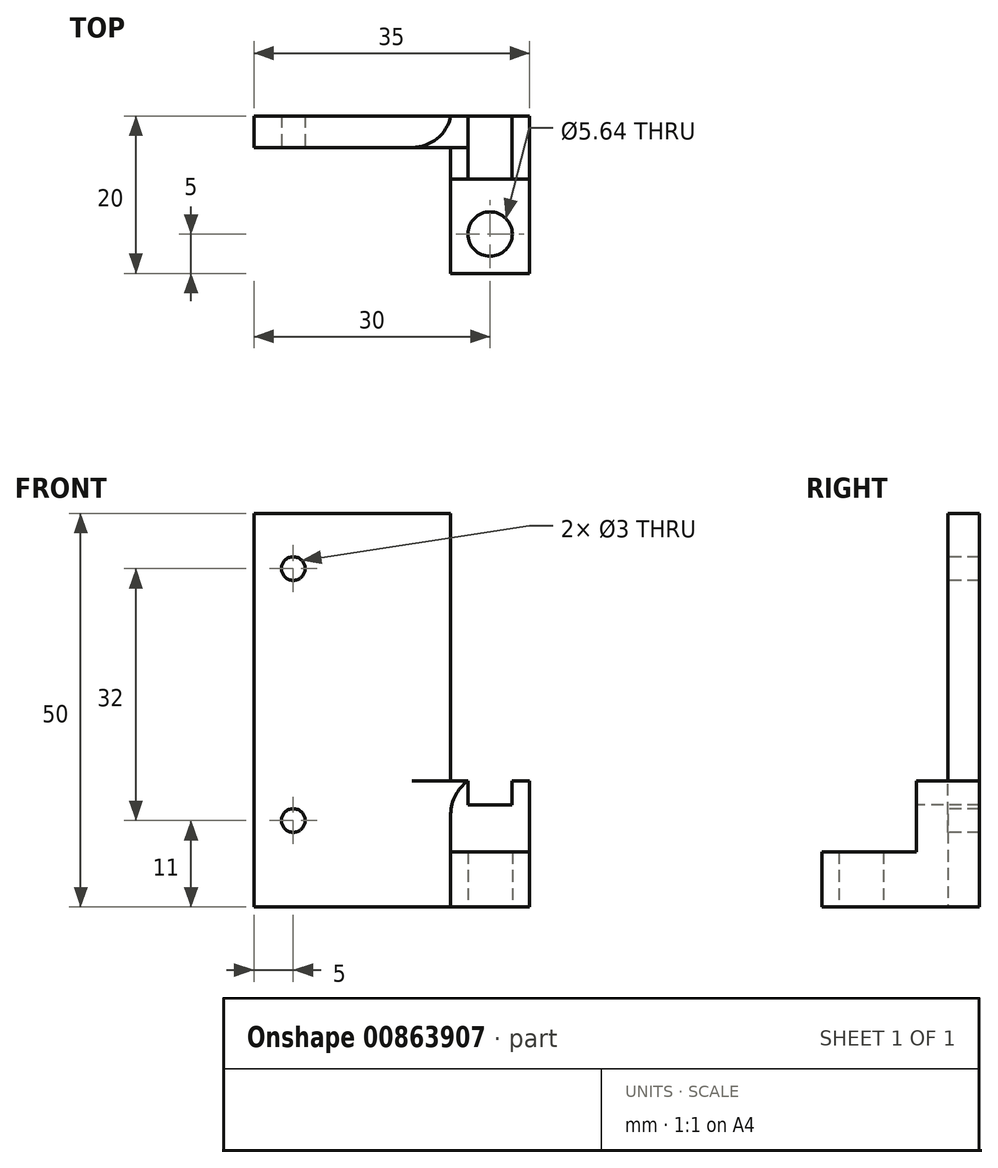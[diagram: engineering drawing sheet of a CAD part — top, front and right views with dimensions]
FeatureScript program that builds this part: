
annotation { "Feature Type Name" : "Feature", "Feature Type Description" : "" }
export const myFeature = defineFeature(function(context is Context, id is Id, definition is map)
    precondition{}
    {
        {
            var Q0;
            Q0=qCreatedBy(makeId("Top.planeOp"),FACE);
            var sketch = newSketch(context, id + "F0", { "sketchPlane" : qUnion([Q0])});
            skLineSegment(sketch, "E0.bottom", {"start": v(0, 0) * mm, "end": v(30, 0) * mm});
            skLineSegment(sketch, "E0.top", {"start": v(0, -20) * mm, "end": v(30, -20) * mm});
            skLineSegment(sketch, "E0.left", {"start": v(0, 0) * mm, "end": v(0, -20) * mm});
            skLineSegment(sketch, "E0.right", {"start": v(30, 0) * mm, "end": v(30, -20) * mm});
            skPoint(sketch, "E1", {"position": v(0, 0) * mm});
            skCircle(sketch, "E2", {"center": v(25, -15) * mm, "radius": 2.82 * mm});
            skSolve(sketch);
        }
        {
            var Q0;
            Q0=makeQuery(id+"F0.imprint","IMPRINT",FACE,{"disambiguationData":[TD([[makeQuery(id+"F0.imprint","IMPRINT",EDGE,{"derivedFrom":sQuery(id+"F0.wireOp",EDGE,"E0.bottom")}),-1.0]])]});
            extrude(context, id + "F1", {"entities" : qUnion([Q0]), "depth" : 16 * mm, "offsetDistance" : 25 * mm});
        }
        {
            var Q0;
            Q0=qCreatedBy(makeId("Top.planeOp"),FACE);
            var sketch = newSketch(context, id + "F2", { "sketchPlane" : qUnion([Q0])});
            skLineSegment(sketch, "E3.top", {"start": v(0, -20) * mm, "end": v(30, -20) * mm});
            skLineSegment(sketch, "E4.0", {"start": v(0, -8) * mm, "end": v(30, -8) * mm});
            skLineSegment(sketch, "E5", {"start": v(0, -8) * mm, "end": v(0, -20) * mm});
            skLineSegment(sketch, "E6", {"start": v(30, -8) * mm, "end": v(30, -20) * mm});
            skSolve(sketch);
        }
        {
            var Q0;
            Q0 = qSketchRegion(id + "F2", true);
            extrude(context, id + "F3", {"entities" : qUnion([Q0]), "depth" : 10 * mm, "offsetDistance" : 25 * mm});
        }
        {
            var Q0;
            Q0=makeQuery(id+"F3.opExtrude","SWEPT_BODY",BODY,{"disambiguationData":[OSD([sQuery(id+"F2.wireOp",EDGE,"E3.top"),sQuery(id+"F2.wireOp",EDGE,"E4.0"),sQuery(id+"F2.wireOp",EDGE,"E5"),sQuery(id+"F2.wireOp",EDGE,"E6")])]});
            transform(context, id + "F4", {"entities" : qUnion([Q0]), "transformType" : TransformType.TRANSLATION_3D, "dx" : 0 * mm, "dy" : 0 * mm, "dz" : 7 * mm, "makeCopy" : false});
        }
        {
            var Q0;
            Q0=makeQuery(id+"F3.opExtrude","SWEPT_BODY",BODY,{"disambiguationData":[OSD([sQuery(id+"F2.wireOp",EDGE,"E3.top"),sQuery(id+"F2.wireOp",EDGE,"E4.0"),sQuery(id+"F2.wireOp",EDGE,"E5"),sQuery(id+"F2.wireOp",EDGE,"E6")])]});
            var Q1;
            Q1=makeQuery(id+"F1.opExtrude","SWEPT_BODY",BODY,{"disambiguationData":[OSD([sQuery(id+"F0.wireOp",EDGE,"E0.bottom"),sQuery(id+"F0.wireOp",EDGE,"E0.top"),sQuery(id+"F0.wireOp",EDGE,"E0.left"),sQuery(id+"F0.wireOp",EDGE,"E0.right"),sQuery(id+"F0.wireOp",EDGE,"E2")])]});
            booleanBodies(context, id + "F5", {"operationType" : BooleanOperationType.SUBTRACTION, "tools" : qUnion([Q0]), "targets" : qUnion([Q1])});
        }
        {
            var Q0;
            Q0=qCreatedBy(makeId("Top.planeOp"),FACE);
            var sketch = newSketch(context, id + "F6", { "sketchPlane" : qUnion([Q0])});
            skLineSegment(sketch, "E7.0", {"start": v(27.8, 0) * mm, "end": v(27.8, -10) * mm});
            skLineSegment(sketch, "E8.0", {"start": v(22.2, 0) * mm, "end": v(22.2, -10) * mm});
            skLineSegment(sketch, "E9", {"start": v(22.2, 0) * mm, "end": v(27.8, 0) * mm});
            skLineSegment(sketch, "E10", {"start": v(22.2, -10) * mm, "end": v(27.8, -10) * mm});
            skSolve(sketch);
        }
        {
            var Q0;
            Q0=makeQuery(id+"F6.imprint","IMPRINT",FACE,{"disambiguationData":[TD([[makeQuery(id+"F6.imprint","IMPRINT",EDGE,{"derivedFrom":sQuery(id+"F6.wireOp",EDGE,"E7.0")}),-1.0]])]});
            extrude(context, id + "F7", {"entities" : qUnion([Q0]), "depth" : 3 * mm, "offsetDistance" : 25 * mm});
        }
        {
            var Q0;
            Q0=makeQuery(id+"F7.opExtrude","SWEPT_BODY",BODY,{"disambiguationData":[OSD([sQuery(id+"F6.wireOp",EDGE,"E7.0"),sQuery(id+"F6.wireOp",EDGE,"E8.0"),sQuery(id+"F6.wireOp",EDGE,"E9"),sQuery(id+"F6.wireOp",EDGE,"E10")])]});
            transform(context, id + "F8", {"entities" : qUnion([Q0]), "transformType" : TransformType.TRANSLATION_3D, "dx" : 0 * mm, "dy" : 0 * mm, "dz" : 13 * mm, "makeCopy" : false});
        }
        {
            var Q0;
            Q0=makeQuery(id+"F7.opExtrude","SWEPT_BODY",BODY,{"disambiguationData":[OSD([sQuery(id+"F6.wireOp",EDGE,"E7.0"),sQuery(id+"F6.wireOp",EDGE,"E8.0"),sQuery(id+"F6.wireOp",EDGE,"E9"),sQuery(id+"F6.wireOp",EDGE,"E10")])]});
            var Q1;
            Q1=makeQuery(id+"F1.opExtrude","SWEPT_BODY",BODY,{"disambiguationData":[OSD([sQuery(id+"F0.wireOp",EDGE,"E0.bottom"),sQuery(id+"F0.wireOp",EDGE,"E0.top"),sQuery(id+"F0.wireOp",EDGE,"E0.left"),sQuery(id+"F0.wireOp",EDGE,"E0.right"),sQuery(id+"F0.wireOp",EDGE,"E2")])]});
            booleanBodies(context, id + "F9", {"operationType" : BooleanOperationType.SUBTRACTION, "tools" : qUnion([Q0]), "targets" : qUnion([Q1])});
        }
        {
            var Q0;
            Q0=qCreatedBy(makeId("Top.planeOp"),FACE);
            var sketch = newSketch(context, id + "F10", { "sketchPlane" : qUnion([Q0])});
            skLineSegment(sketch, "E11", {"start": v(0, 0) * mm, "end": v(-5, 0) * mm});
            skLineSegment(sketch, "E12", {"start": v(0, 0) * mm, "end": v(20, 0) * mm});
            skLineSegment(sketch, "E13", {"start": v(-5, 0) * mm, "end": v(-5, -4) * mm});
            skLineSegment(sketch, "E14", {"start": v(20, 0) * mm, "end": v(20, -4) * mm});
            skLineSegment(sketch, "E15", {"start": v(-5, -4) * mm, "end": v(20, -4) * mm});
            skSolve(sketch);
        }
        {
            var Q0;
            Q0=makeQuery(id+"F10.imprint","IMPRINT",FACE,{"disambiguationData":[TD([[makeQuery(id+"F10.imprint","IMPRINT",EDGE,{"derivedFrom":sQuery(id+"F10.wireOp",EDGE,"E11")}),1.0]])]});
            extrude(context, id + "F11", {"entities" : qUnion([Q0]), "depth" : 50 * mm, "offsetDistance" : 25 * mm});
        }
        {
            var Q0;
            Q0=qCreatedBy(makeId("Top.planeOp"),FACE);
            var sketch = newSketch(context, id + "F12", { "sketchPlane" : qUnion([Q0])});
            skLineSegment(sketch, "E16.bottom", {"start": v(0, 0) * mm, "end": v(20, 0) * mm});
            skLineSegment(sketch, "E16.top", {"start": v(0, -25) * mm, "end": v(20, -25) * mm});
            skLineSegment(sketch, "E16.left", {"start": v(0, 0) * mm, "end": v(0, -25) * mm});
            skLineSegment(sketch, "E16.right", {"start": v(20, 0) * mm, "end": v(20, -25) * mm});
            skSolve(sketch);
        }
        {
            var Q0;
            Q0=makeQuery(id+"F12.imprint","IMPRINT",FACE,{"disambiguationData":[TD([[makeQuery(id+"F12.imprint","IMPRINT",EDGE,{"derivedFrom":sQuery(id+"F12.wireOp",EDGE,"E16.bottom")}),-1.0]])]});
            extrude(context, id + "F13", {"entities" : qUnion([Q0]), "depth" : 25 * mm, "offsetDistance" : 25 * mm});
        }
        {
            var Q0;
            Q0=makeQuery(id+"F13.opExtrude","SWEPT_BODY",BODY,{"disambiguationData":[OSD([sQuery(id+"F12.wireOp",EDGE,"E16.bottom"),sQuery(id+"F12.wireOp",EDGE,"E16.top"),sQuery(id+"F12.wireOp",EDGE,"E16.left"),sQuery(id+"F12.wireOp",EDGE,"E16.right")])]});
            var Q1;
            Q1=makeQuery(id+"F1.opExtrude","SWEPT_BODY",BODY,{"disambiguationData":[OSD([sQuery(id+"F0.wireOp",EDGE,"E0.bottom"),sQuery(id+"F0.wireOp",EDGE,"E0.top"),sQuery(id+"F0.wireOp",EDGE,"E0.left"),sQuery(id+"F0.wireOp",EDGE,"E0.right"),sQuery(id+"F0.wireOp",EDGE,"E2")])]});
            booleanBodies(context, id + "F14", {"operationType" : BooleanOperationType.SUBTRACTION, "tools" : qUnion([Q0]), "targets" : qUnion([Q1])});
        }
        {
            var Q0;
            Q0=makeQuery(id+"F11.opExtrude","SWEPT_BODY",BODY,{"disambiguationData":[OSD([sQuery(id+"F10.wireOp",EDGE,"E11"),sQuery(id+"F10.wireOp",EDGE,"E12"),sQuery(id+"F10.wireOp",EDGE,"E13"),sQuery(id+"F10.wireOp",EDGE,"E14"),sQuery(id+"F10.wireOp",EDGE,"E15")])]});
            var Q1;
            Q1=makeQuery(id+"F1.opExtrude","SWEPT_BODY",BODY,{"disambiguationData":[OSD([sQuery(id+"F0.wireOp",EDGE,"E0.bottom"),sQuery(id+"F0.wireOp",EDGE,"E0.top"),sQuery(id+"F0.wireOp",EDGE,"E0.left"),sQuery(id+"F0.wireOp",EDGE,"E0.right"),sQuery(id+"F0.wireOp",EDGE,"E2")])]});
            booleanBodies(context, id + "F15", {"operationType" : BooleanOperationType.UNION, "tools" : qUnion([Q0, Q1])});
        }
        {
            var Q0;
            {var subQ0=sQuery(id+"F10.wireOp",EDGE,"E15");Q0=makeQuery(id+"F15.opBoolean","SPLIT",EDGE,{"disambiguationData":[topologyDisambiguationEdgeConnected([makeQuery(id+"F14.opBoolean","COPY",FACE,{"derivedFrom":makeQuery(id+"F13.opExtrude","SWEPT_FACE",FACE,{"disambiguationData":[OSD([sQuery(id+"F12.wireOp",EDGE,"E16.right")])]})})])],"derivedFrom":makeQuery(id+"F11.opExtrude","SWEPT_EDGE",EDGE,{"disambiguationData":[OSD([sQuery(id+"F10.wireOp",EDGE,"E14"),subQ0])]})});}
            fillet(context, id + "F16", {"entities" : qUnion([Q0]), "radius" : 5 * mm, "tangentPropagation" : true, "allowEdgeOverflow" : false});
        }
        {
            var Q0;
            {var subQ0=sQuery(id+"F0.wireOp",EDGE,"E0.bottom");var subQ1=sQuery(id+"F0.wireOp",EDGE,"E0.left");Q0=makeQuery(id+"F16.opFillet","TWEAK_EDGE",EDGE,{"derivedFrom":[makeQuery(id+"F15.opBoolean","TWEAK_VERTEX",VERTEX,{"derivedFrom":[makeQuery(id+"F11.opExtrude","SWEPT_FACE",FACE,{"disambiguationData":[OSD([sQuery(id+"F10.wireOp",EDGE,"E14")])]}),makeQuery(id+"F11.opExtrude","SWEPT_FACE",FACE,{"disambiguationData":[OSD([sQuery(id+"F10.wireOp",EDGE,"E15")])]}),makeQuery(id+"F14.opBoolean","COPY",FACE,{"derivedFrom":makeQuery(id+"F13.opExtrude","SWEPT_FACE",FACE,{"disambiguationData":[OSD([sQuery(id+"F12.wireOp",EDGE,"E16.right")])]})}),makeQuery(id+"F9.opBoolean","SPLIT",FACE,{"disambiguationData":[TD([makeQuery(id+"F1.opExtrude","SWEPT_FACE",FACE,{"disambiguationData":[OSD([subQ1])]})])],"derivedFrom":makeQuery(id+"F1.opExtrude","CAP_FACE",FACE,{"disambiguationData":[OSD([subQ0,sQuery(id+"F0.wireOp",EDGE,"E0.top"),subQ1,sQuery(id+"F0.wireOp",EDGE,"E0.right"),sQuery(id+"F0.wireOp",EDGE,"E2")])],"isStart":false})})]})]});}
            var Q1;
            {var subQ0=sQuery(id+"F0.wireOp",EDGE,"E0.left");var subQ1=sQuery(id+"F0.wireOp",EDGE,"E0.bottom");var subQ2=makeQuery(id+"F1.opExtrude","CAP_FACE",FACE,{"disambiguationData":[OSD([subQ1,sQuery(id+"F0.wireOp",EDGE,"E0.top"),subQ0,sQuery(id+"F0.wireOp",EDGE,"E0.right"),sQuery(id+"F0.wireOp",EDGE,"E2")])],"isStart":false});Q1=makeQuery(id+"F15.opBoolean","SPLIT",EDGE,{"disambiguationData":[topologyDisambiguationEdgeConnected([makeQuery(id+"F11.opExtrude","SWEPT_FACE",FACE,{"disambiguationData":[OSD([sQuery(id+"F10.wireOp",EDGE,"E14")])]})])],"derivedFrom":makeQuery(id+"F14.opBoolean","INTERSECT",EDGE,{"derivedFrom":[makeQuery(id+"F9.opBoolean","SPLIT",FACE,{"disambiguationData":[TD([makeQuery(id+"F1.opExtrude","SWEPT_FACE",FACE,{"disambiguationData":[OSD([subQ0])]})])],"derivedFrom":subQ2}),makeQuery(id+"F13.opExtrude","SWEPT_FACE",FACE,{"disambiguationData":[OSD([sQuery(id+"F12.wireOp",EDGE,"E16.right")])]})]})});}
            fillet(context, id + "F17", {"entities" : qUnion([Q0, Q1]), "radius" : 5 * mm, "tangentPropagation" : true, "allowEdgeOverflow" : false});
        }
        {
            var Q0;
            Q0=makeQuery(id+"F11.opExtrude","SWEPT_FACE",FACE,{"disambiguationData":[OSD([sQuery(id+"F10.wireOp",EDGE,"E15")])]});
            var sketch = newSketch(context, id + "F18", { "sketchPlane" : qUnion([Q0])});
            skPoint(sketch, "E17", {"position": v(0, 43) * mm});
            skPoint(sketch, "E18", {"position": v(0, 11) * mm});
            skSolve(sketch);
        }
        {
            var Q0;
            Q0=sQuery(id+"F18.wireOp",VERTEX,"E17");
            var Q1;
            Q1=makeQuery(id+"F11.opExtrude","SWEPT_BODY",BODY,{"disambiguationData":[OSD([sQuery(id+"F10.wireOp",EDGE,"E11"),sQuery(id+"F10.wireOp",EDGE,"E12"),sQuery(id+"F10.wireOp",EDGE,"E13"),sQuery(id+"F10.wireOp",EDGE,"E14"),sQuery(id+"F10.wireOp",EDGE,"E15")])]});
            hole(context, id + "F19", {"style" : HoleStyle.SIMPLE, "endStyle" : HoleEndStyle.THROUGH, "holeDiameter" : 3 * mm, "majorDiameter" : 5 * mm, "isTappedThrough" : true, "tappedDepth" : 12 * mm, "tapClearance" : 3, "locations" : qUnion([Q0]), "scope" : qUnion([Q1])});
        }
        {
            var Q0;
            Q0=sQuery(id+"F18.wireOp",VERTEX,"E18");
            var Q1;
            Q1=makeQuery(id+"F11.opExtrude","SWEPT_BODY",BODY,{"disambiguationData":[OSD([sQuery(id+"F10.wireOp",EDGE,"E11"),sQuery(id+"F10.wireOp",EDGE,"E12"),sQuery(id+"F10.wireOp",EDGE,"E13"),sQuery(id+"F10.wireOp",EDGE,"E14"),sQuery(id+"F10.wireOp",EDGE,"E15")])]});
            hole(context, id + "F20", {"style" : HoleStyle.SIMPLE, "endStyle" : HoleEndStyle.THROUGH, "holeDiameter" : 3 * mm, "majorDiameter" : 5 * mm, "isTappedThrough" : true, "tappedDepth" : 12 * mm, "tapClearance" : 3, "locations" : qUnion([Q0]), "scope" : qUnion([Q1])});
        }
    });
